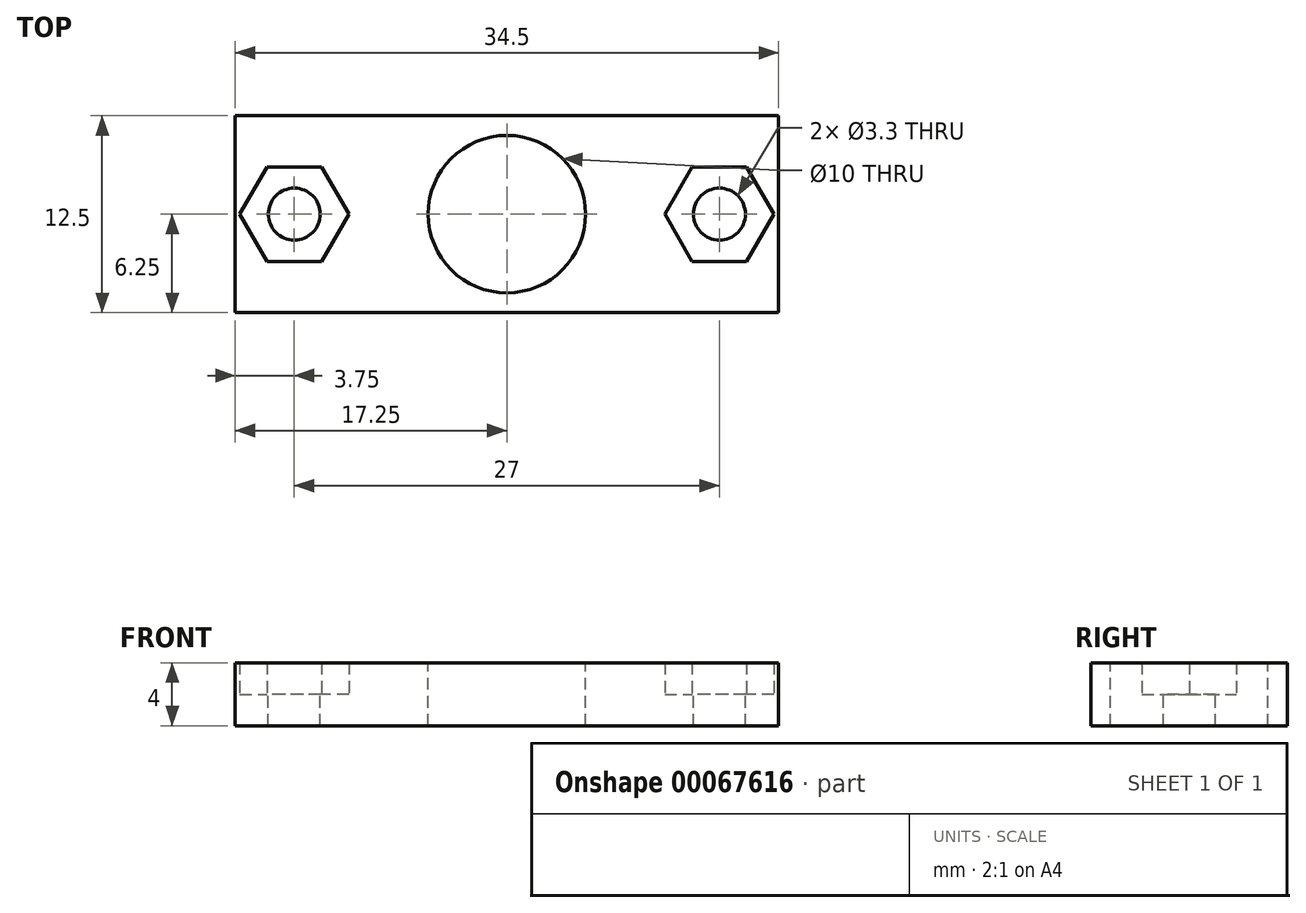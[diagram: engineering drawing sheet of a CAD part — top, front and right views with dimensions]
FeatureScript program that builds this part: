
annotation { "Feature Type Name" : "Feature", "Feature Type Description" : "" }
export const myFeature = defineFeature(function(context is Context, id is Id, definition is map)
    precondition{}
    {
        {
            var Q0;
            Q0=qCreatedBy(makeId("Top.planeOp"),FACE);
            var sketch = newSketch(context, id + "F0", { "sketchPlane" : qUnion([Q0])});
            skLineSegment(sketch, "E0.bottom", {"start": v(-17.25, 6.25) * mm, "end": v(17.25, 6.25) * mm});
            skLineSegment(sketch, "E0.top", {"start": v(-17.25, -6.25) * mm, "end": v(17.25, -6.25) * mm});
            skLineSegment(sketch, "E0.left", {"start": v(-17.25, 6.25) * mm, "end": v(-17.25, -6.25) * mm});
            skLineSegment(sketch, "E0.right", {"start": v(17.25, 6.25) * mm, "end": v(17.25, -6.25) * mm});
            skPoint(sketch, "E0.middle", {"position": v(0, 0) * mm});
            skCircle(sketch, "E1", {"center": v(0, 0) * mm, "radius": 5 * mm});
            skCircle(sketch, "E2.cCircle", {"center": v(-13.5, 0) * mm, "radius": 3 * mm, "construction": true});
            skLineSegment(sketch, "E2.0", {"start": v(-15.23, 3) * mm, "end": v(-11.77, 3) * mm});
            skLineSegment(sketch, "E2.1", {"start": v(-11.77, 3) * mm, "end": v(-10.04, 0) * mm});
            skLineSegment(sketch, "E2.2", {"start": v(-10.04, 0) * mm, "end": v(-11.77, -3) * mm});
            skLineSegment(sketch, "E2.3", {"start": v(-11.77, -3) * mm, "end": v(-15.23, -3) * mm});
            skLineSegment(sketch, "E2.4", {"start": v(-15.23, -3) * mm, "end": v(-16.96, 0) * mm});
            skLineSegment(sketch, "E2.5", {"start": v(-16.96, 0) * mm, "end": v(-15.23, 3) * mm});
            skPoint(sketch, "E2.0.midPoint", {"position": v(-13.5, 3) * mm});
            skCircle(sketch, "E3.cCircle", {"center": v(13.5, 0) * mm, "radius": 3 * mm, "construction": true});
            skLineSegment(sketch, "E3.0", {"start": v(11.77, 3) * mm, "end": v(15.23, 3) * mm});
            skLineSegment(sketch, "E3.1", {"start": v(15.23, 3) * mm, "end": v(16.96, 0) * mm});
            skLineSegment(sketch, "E3.2", {"start": v(16.96, 0) * mm, "end": v(15.23, -3) * mm});
            skLineSegment(sketch, "E3.3", {"start": v(15.23, -3) * mm, "end": v(11.77, -3) * mm});
            skLineSegment(sketch, "E3.4", {"start": v(11.77, -3) * mm, "end": v(10.04, 0) * mm});
            skLineSegment(sketch, "E3.5", {"start": v(10.04, 0) * mm, "end": v(11.77, 3) * mm});
            skPoint(sketch, "E3.0.midPoint", {"position": v(13.5, 3) * mm});
            skCircle(sketch, "E4", {"center": v(-13.5, 0) * mm, "radius": 1.65 * mm});
            skCircle(sketch, "E5", {"center": v(13.5, 0) * mm, "radius": 1.65 * mm});
            skSolve(sketch);
        }
        {
            var Q0;
            Q0=makeQuery(id+"F0.imprint","IMPRINT",FACE,{"disambiguationData":[TD([[makeQuery(id+"F0.imprint","IMPRINT",EDGE,{"derivedFrom":sQuery(id+"F0.wireOp",EDGE,"E2.0")}),-1.0]])]});
            var Q1;
            Q1=makeQuery(id+"F0.imprint","IMPRINT",FACE,{"disambiguationData":[TD([[makeQuery(id+"F0.imprint","IMPRINT",EDGE,{"derivedFrom":sQuery(id+"F0.wireOp",EDGE,"E0.bottom")}),-1.0]])]});
            var Q2;
            Q2=makeQuery(id+"F0.imprint","IMPRINT",FACE,{"disambiguationData":[TD([[makeQuery(id+"F0.imprint","IMPRINT",EDGE,{"derivedFrom":sQuery(id+"F0.wireOp",EDGE,"E3.0")}),-1.0]])]});
            extrude(context, id + "F1", {"entities" : qUnion([Q0, Q1, Q2]), "oppositeDirection" : true, "depth" : 2 * mm});
        }
        {
            var Q0;
            Q0=makeQuery(id+"F0.imprint","IMPRINT",FACE,{"disambiguationData":[TD([[makeQuery(id+"F0.imprint","IMPRINT",EDGE,{"derivedFrom":sQuery(id+"F0.wireOp",EDGE,"E0.bottom")}),-1.0]])]});
            extrude(context, id + "F2", {"entities" : qUnion([Q0]), "operationType" : NewBodyOperationType.ADD, "depth" : 2 * mm});
        }
    });
